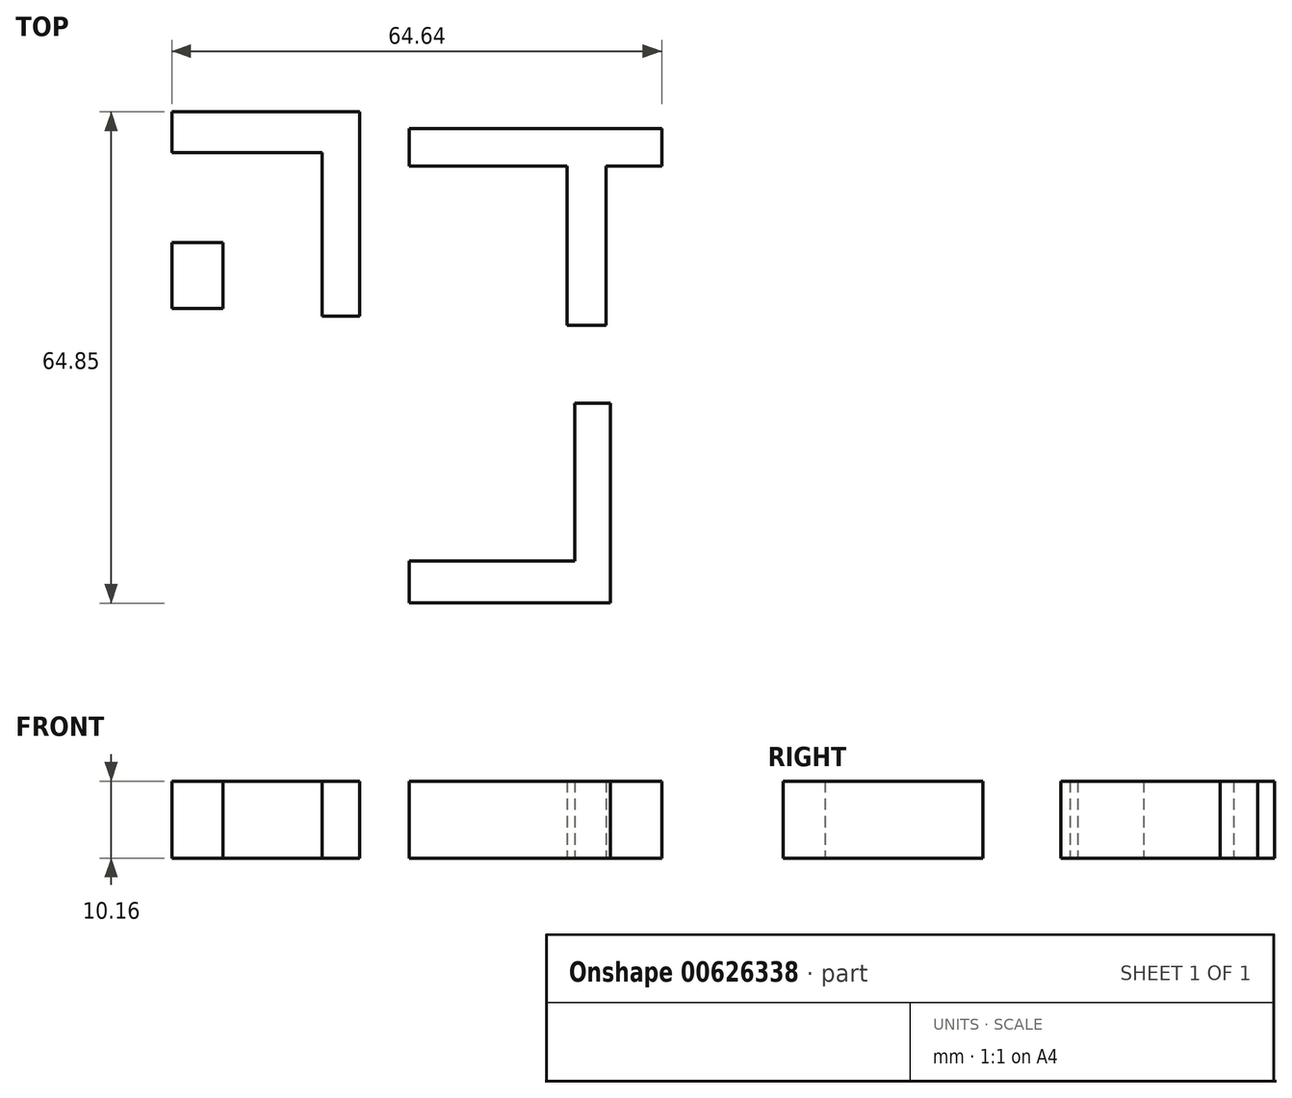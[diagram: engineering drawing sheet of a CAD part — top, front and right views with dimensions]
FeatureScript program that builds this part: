
annotation { "Feature Type Name" : "Feature", "Feature Type Description" : "" }
export const myFeature = defineFeature(function(context is Context, id is Id, definition is map)
    precondition{}
    {
        {
            var Q0;
            Q0=qCreatedBy(makeId("Top.planeOp"),FACE);
            var sketch = newSketch(context, id + "F0", { "sketchPlane" : qUnion([Q0])});
            skLineSegment(sketch, "E0.bottom", {"start": v(-9.22, 41.24) * mm, "end": v(24.1, 41.24) * mm});
            skLineSegment(sketch, "E0.top", {"start": v(-9.22, 36.29) * mm, "end": v(11.6, 36.29) * mm});
            skLineSegment(sketch, "E0.left", {"start": v(-9.22, 41.24) * mm, "end": v(-9.22, 36.29) * mm});
            skLineSegment(sketch, "E0.right", {"start": v(24.1, 41.24) * mm, "end": v(24.1, 36.29) * mm});
            skLineSegment(sketch, "E1.top", {"start": v(16.76, 15.27) * mm, "end": v(11.6, 15.27) * mm});
            skLineSegment(sketch, "E1.left", {"start": v(16.76, 36.29) * mm, "end": v(16.76, 15.27) * mm});
            skLineSegment(sketch, "E1.right", {"start": v(11.6, 36.29) * mm, "end": v(11.6, 15.27) * mm});
            skLineSegment(sketch, "E2.trimOffspring", {"start": v(16.76, 36.29) * mm, "end": v(24.1, 36.29) * mm});
            skLineSegment(sketch, "E3.bottom", {"start": v(17.35, 4.96) * mm, "end": v(12.6, 4.96) * mm});
            skLineSegment(sketch, "E3.top", {"start": v(17.35, -21.42) * mm, "end": v(12.6, -21.42) * mm});
            skLineSegment(sketch, "E3.left", {"start": v(17.35, 4.96) * mm, "end": v(17.35, -21.42) * mm});
            skLineSegment(sketch, "E3.right", {"start": v(12.6, 4.96) * mm, "end": v(12.6, -15.86) * mm});
            skLineSegment(sketch, "E4.bottom", {"start": v(-9.22, -21.42) * mm, "end": v(17.35, -21.42) * mm});
            skLineSegment(sketch, "E4.top", {"start": v(-9.22, -15.86) * mm, "end": v(12.6, -15.86) * mm});
            skLineSegment(sketch, "E4.left", {"start": v(-9.22, -21.42) * mm, "end": v(-9.22, -15.86) * mm});
            skLineSegment(sketch, "E4.right", {"start": v(17.35, -21.42) * mm, "end": v(17.35, -15.86) * mm});
            skLineSegment(sketch, "E5.bottom", {"start": v(-40.55, 43.43) * mm, "end": v(-20.72, 43.43) * mm});
            skLineSegment(sketch, "E5.top", {"start": v(-40.55, 38.07) * mm, "end": v(-20.72, 38.07) * mm});
            skLineSegment(sketch, "E6.left", {"start": v(-20.72, 38.07) * mm, "end": v(-20.72, 16.46) * mm});
            skLineSegment(sketch, "E6.right", {"start": v(-15.76, 43.43) * mm, "end": v(-15.76, 16.46) * mm});
            skLineSegment(sketch, "E7", {"start": v(-20.72, 43.43) * mm, "end": v(-15.76, 43.43) * mm});
            skLineSegment(sketch, "E8", {"start": v(-20.72, 16.46) * mm, "end": v(-15.76, 16.46) * mm});
            skLineSegment(sketch, "E9", {"start": v(-40.55, 43.43) * mm, "end": v(-40.55, 38.07) * mm});
            skLineSegment(sketch, "E10.bottom", {"start": v(-40.55, 17.45) * mm, "end": v(-33.8, 17.45) * mm});
            skLineSegment(sketch, "E10.top", {"start": v(-40.55, 26.17) * mm, "end": v(-33.8, 26.17) * mm});
            skLineSegment(sketch, "E10.left", {"start": v(-40.55, 17.45) * mm, "end": v(-40.55, 26.17) * mm});
            skLineSegment(sketch, "E10.right", {"start": v(-33.8, 17.45) * mm, "end": v(-33.8, 26.17) * mm});
            skSolve(sketch);
        }
        {
            var Q0;
            Q0 = qSketchRegion(id + "F0", true);
            extrude(context, id + "F1", {"entities" : qUnion([Q0]), "depth" : 10.16 * mm, "offsetDistance" : 25.4 * mm});
        }
    });
